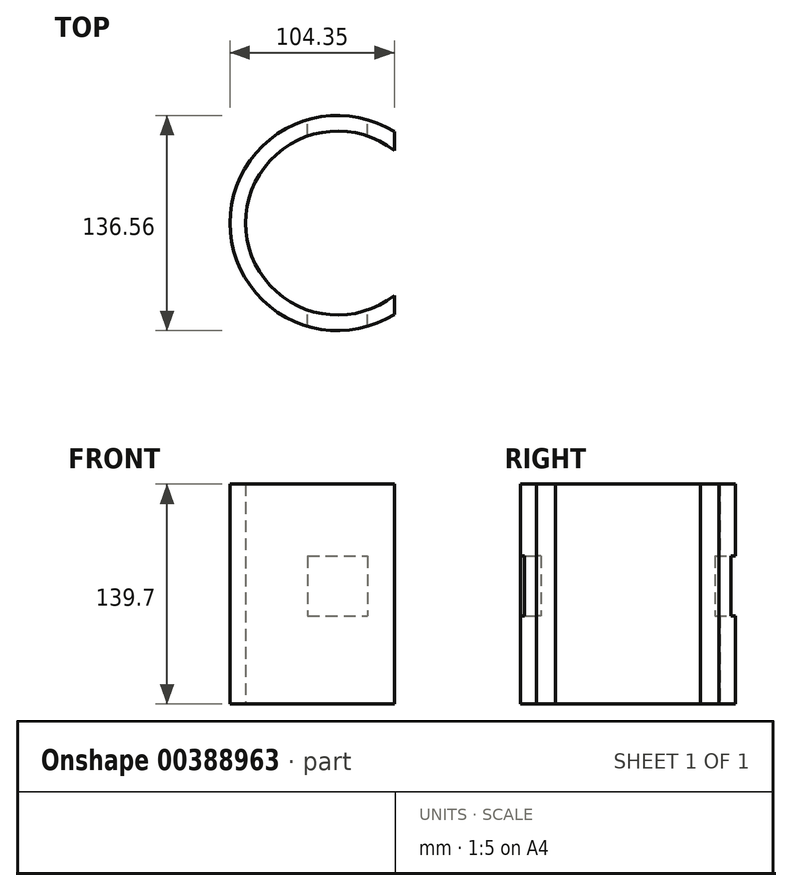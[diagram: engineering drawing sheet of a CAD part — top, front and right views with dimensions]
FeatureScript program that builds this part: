
annotation { "Feature Type Name" : "Feature", "Feature Type Description" : "" }
export const myFeature = defineFeature(function(context is Context, id is Id, definition is map)
    precondition{}
    {
        {
            var Q0;
            Q0=qCreatedBy(makeId("Top.planeOp"),FACE);
            var sketch = newSketch(context, id + "F0", { "sketchPlane" : qUnion([Q0])});
            skCircle(sketch, "E0", {"center": v(0, 0) * mm, "radius": 58.42 * mm});
            skCircle(sketch, "E1", {"center": v(0, 0) * mm, "radius": 68.28 * mm});
            skSolve(sketch);
        }
        {
            var Q0;
            Q0 = qSketchRegion(id + "F0", true);
            extrude(context, id + "F1", {"entities" : qUnion([Q0]), "depth" : 139.7 * mm});
        }
        {
            var Q0;
            Q0=qCreatedBy(makeId("Front.planeOp"),FACE);
            var sketch = newSketch(context, id + "F2", { "sketchPlane" : qUnion([Q0])});
            skLineSegment(sketch, "E2.bottom", {"start": v(19.05, 55.83) * mm, "end": v(-19.05, 55.83) * mm});
            skLineSegment(sketch, "E2.top", {"start": v(19.05, 93.93) * mm, "end": v(-19.05, 93.93) * mm});
            skLineSegment(sketch, "E2.left", {"start": v(19.05, 55.83) * mm, "end": v(19.05, 93.93) * mm});
            skLineSegment(sketch, "E2.right", {"start": v(-19.05, 55.83) * mm, "end": v(-19.05, 93.93) * mm});
            skPoint(sketch, "E2.middle", {"position": v(0, 74.88) * mm});
            skSolve(sketch);
        }
        {
            var Q0;
            Q0 = qSketchRegion(id + "F2", true);
            extrude(context, id + "F3", {"entities" : qUnion([Q0]), "operationType" : NewBodyOperationType.REMOVE, "endBound" : BoundingType.THROUGH_ALL, "depth" : 25.4 * mm, "hasSecondDirection" : true, "secondDirectionBound" : SecondDirectionBoundingType.THROUGH_ALL, "secondDirectionOppositeDirection" : true, "secondDirectionDepth" : 25.4 * mm});
        }
        {
            var Q0;
            Q0=qCreatedBy(makeId("Top.planeOp"),FACE);
            var sketch = newSketch(context, id + "F4", { "sketchPlane" : qUnion([Q0])});
            skLineSegment(sketch, "E3.bottom", {"start": v(36.07, 72.57) * mm, "end": v(146.4, 72.57) * mm});
            skLineSegment(sketch, "E3.top", {"start": v(36.07, -72.57) * mm, "end": v(146.4, -72.57) * mm});
            skLineSegment(sketch, "E3.left", {"start": v(36.07, 72.57) * mm, "end": v(36.07, -72.57) * mm});
            skLineSegment(sketch, "E3.right", {"start": v(146.4, 72.57) * mm, "end": v(146.4, -72.57) * mm});
            skPoint(sketch, "E3.middle", {"position": v(91.24, 0) * mm});
            skSolve(sketch);
        }
        {
            var Q0;
            Q0=makeQuery(id+"F4.imprint","IMPRINT",FACE,{"disambiguationData":[TD([[makeQuery(id+"F4.imprint","IMPRINT",EDGE,{"derivedFrom":sQuery(id+"F4.wireOp",EDGE,"E3.bottom")}),-1.0]])]});
            extrude(context, id + "F5", {"entities" : qUnion([Q0]), "operationType" : NewBodyOperationType.REMOVE, "endBound" : BoundingType.THROUGH_ALL, "oppositeDirection" : true, "depth" : 25.4 * mm, "hasSecondDirection" : true, "secondDirectionBound" : SecondDirectionBoundingType.THROUGH_ALL, "secondDirectionOppositeDirection" : false, "secondDirectionDepth" : 25.4 * mm});
        }
    });
